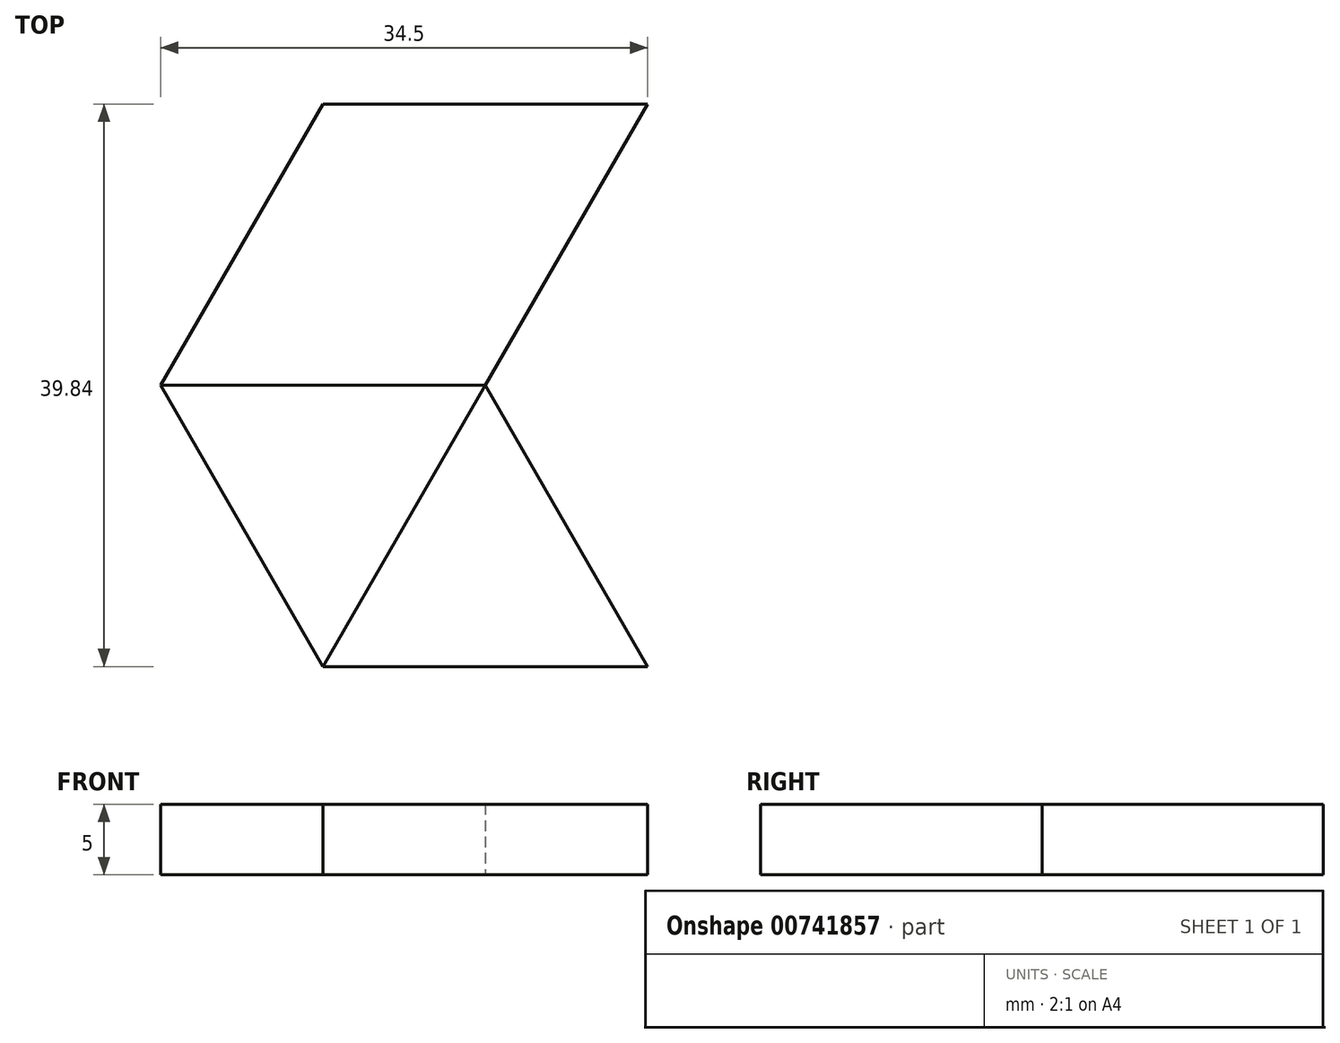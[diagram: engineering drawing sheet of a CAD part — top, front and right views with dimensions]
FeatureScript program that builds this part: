
annotation { "Feature Type Name" : "Feature", "Feature Type Description" : "" }
export const myFeature = defineFeature(function(context is Context, id is Id, definition is map)
    precondition{}
    {
        {
            var Q0;
            Q0=qCreatedBy(makeId("Top.planeOp"),FACE);
            var sketch = newSketch(context, id + "F0", { "sketchPlane" : qUnion([Q0])});
            skCircle(sketch, "E0.cCircle", {"center": v(0, 0) * mm, "radius": 6.64 * mm, "construction": true});
            skLineSegment(sketch, "E0.0", {"start": v(0, 13.28) * mm, "end": v(11.5, -6.64) * mm});
            skLineSegment(sketch, "E0.1", {"start": v(11.5, -6.64) * mm, "end": v(-11.5, -6.64) * mm});
            skLineSegment(sketch, "E0.2", {"start": v(-11.5, -6.64) * mm, "end": v(0, 13.28) * mm});
            skPoint(sketch, "E0.0.midPoint", {"position": v(5.75, 3.32) * mm});
            skLineSegment(sketch, "E1.MirrorCS", {"start": v(23, 13.28) * mm, "end": v(0, 13.28) * mm});
            skLineSegment(sketch, "E2.MirrorCS", {"start": v(11.5, -6.64) * mm, "end": v(23, 13.28) * mm});
            skLineSegment(sketch, "E3.MirrorCS", {"start": v(-11.5, -6.64) * mm, "end": v(0, -26.56) * mm});
            skLineSegment(sketch, "E4.MirrorCS", {"start": v(0, -26.56) * mm, "end": v(11.5, -6.64) * mm});
            skLineSegment(sketch, "E5.MirrorCS", {"start": v(23, -26.56) * mm, "end": v(0, -26.56) * mm});
            skLineSegment(sketch, "E6.MirrorCS", {"start": v(11.5, -6.64) * mm, "end": v(23, -26.56) * mm});
            skLineSegment(sketch, "E7", {"start": v(23, 13.28) * mm, "end": v(23, -26.56) * mm, "construction": true});
            skSolve(sketch);
        }
        {
            var Q0;
            Q0=makeQuery(id+"F0.imprint","IMPRINT",FACE,{"disambiguationData":[TD([[makeQuery(id+"F0.imprint","IMPRINT",EDGE,{"derivedFrom":sQuery(id+"F0.wireOp",EDGE,"E4.MirrorCS")}),-1.0]])]});
            var Q1;
            Q1=makeQuery(id+"F0.imprint","IMPRINT",FACE,{"disambiguationData":[TD([[makeQuery(id+"F0.imprint","IMPRINT",EDGE,{"derivedFrom":sQuery(id+"F0.wireOp",EDGE,"E0.0")}),-1.0]])]});
            var Q2;
            Q2=makeQuery(id+"F0.imprint","IMPRINT",FACE,{"disambiguationData":[TD([[makeQuery(id+"F0.imprint","IMPRINT",EDGE,{"derivedFrom":sQuery(id+"F0.wireOp",EDGE,"E0.1")}),1.0]])]});
            var Q3;
            Q3=makeQuery(id+"F0.imprint","IMPRINT",FACE,{"disambiguationData":[TD([[makeQuery(id+"F0.imprint","IMPRINT",EDGE,{"derivedFrom":sQuery(id+"F0.wireOp",EDGE,"E0.0")}),1.0]])]});
            extrude(context, id + "F1", {"entities" : qUnion([Q0, Q1, Q2, Q3]), "depth" : 5 * mm, "offsetDistance" : 25 * mm});
        }
        {
            var Q0;
            Q0=makeQuery(id+"F0.imprint","IMPRINT",FACE,{"disambiguationData":[TD([[makeQuery(id+"F0.imprint","IMPRINT",EDGE,{"derivedFrom":sQuery(id+"F0.wireOp",EDGE,"E4.MirrorCS")}),-1.0]])]});
            var Q1;
            Q1=makeQuery(id+"F0.imprint","IMPRINT",FACE,{"disambiguationData":[TD([[makeQuery(id+"F0.imprint","IMPRINT",EDGE,{"derivedFrom":sQuery(id+"F0.wireOp",EDGE,"E0.1")}),1.0]])]});
            extrude(context, id + "F2", {"entities" : qUnion([Q0, Q1]), "depth" : 5 * mm, "offsetDistance" : 25 * mm});
        }
        {
            var Q0;
            Q0=makeQuery(id+"F0.imprint","IMPRINT",FACE,{"disambiguationData":[TD([[makeQuery(id+"F0.imprint","IMPRINT",EDGE,{"derivedFrom":sQuery(id+"F0.wireOp",EDGE,"E0.1")}),1.0]])]});
            extrude(context, id + "F3", {"entities" : qUnion([Q0]), "depth" : 5 * mm, "offsetDistance" : 25 * mm});
        }
    });
